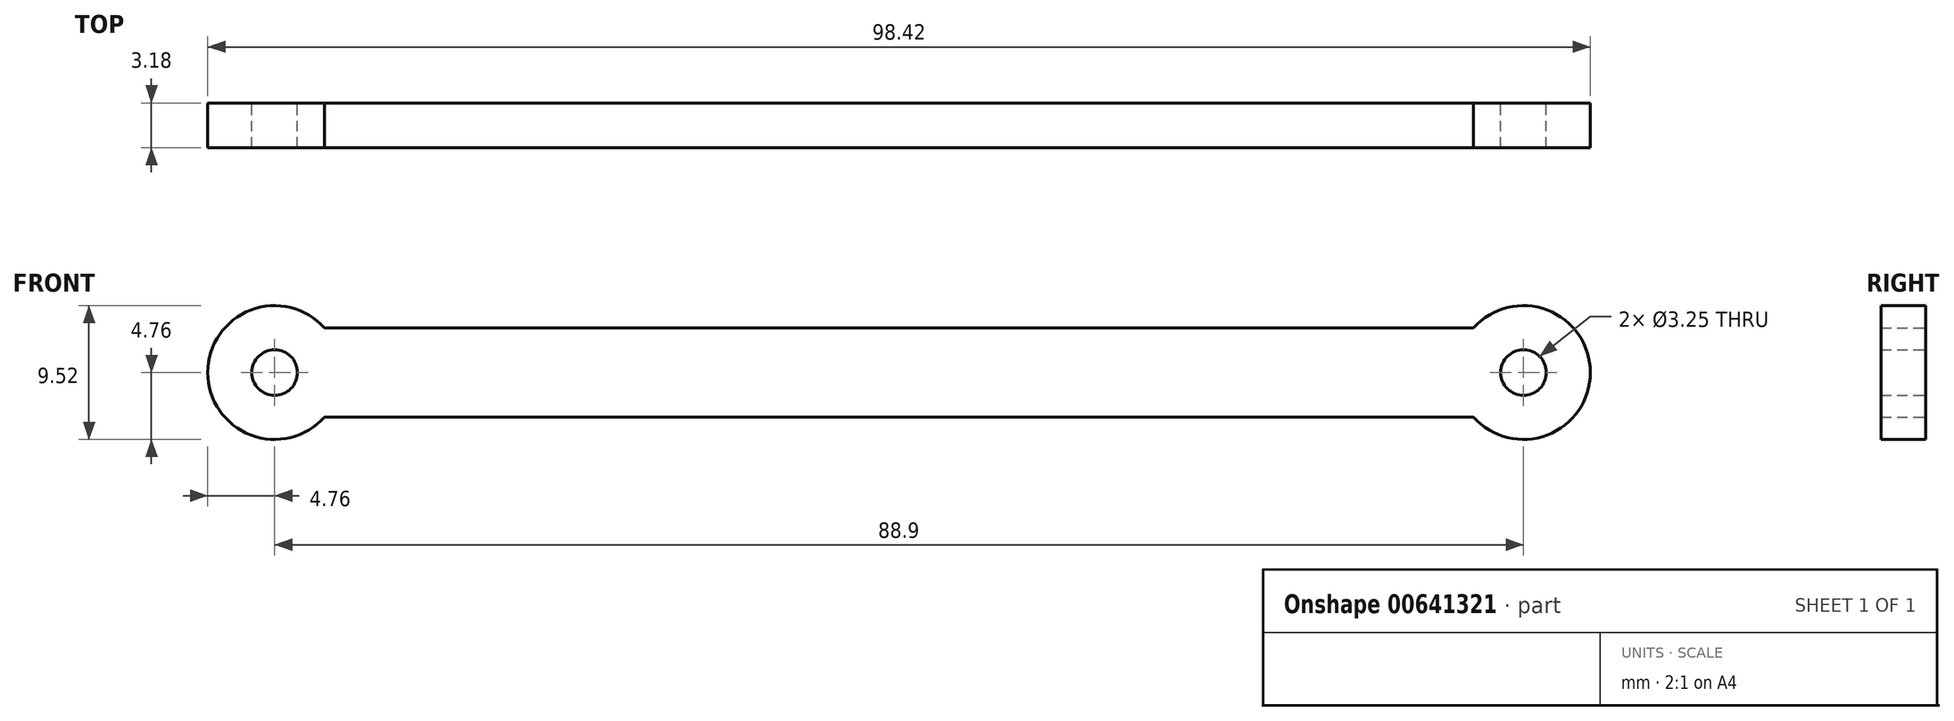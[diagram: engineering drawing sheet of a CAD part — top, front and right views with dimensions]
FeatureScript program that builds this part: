
annotation { "Feature Type Name" : "Feature", "Feature Type Description" : "" }
export const myFeature = defineFeature(function(context is Context, id is Id, definition is map)
    precondition{}
    {
        {
            var Q0;
            Q0=qCreatedBy(makeId("Front.planeOp"),FACE);
            var sketch = newSketch(context, id + "F0", { "sketchPlane" : qUnion([Q0])});
            skLineSegment(sketch, "E0", {"start": v(0, 0) * mm, "end": v(88.9, 0) * mm});
            skCircle(sketch, "E1", {"center": v(0, 0) * mm, "radius": 4.76 * mm});
            skCircle(sketch, "E2", {"center": v(88.9, 0) * mm, "radius": 4.76 * mm});
            skLineSegment(sketch, "E3.0", {"start": v(3.55, 3.18) * mm, "end": v(85.35, 3.18) * mm});
            skLineSegment(sketch, "E4.MirrorCS", {"start": v(3.55, -3.18) * mm, "end": v(85.35, -3.18) * mm});
            skPoint(sketch, "E5.orphan", {"position": v(88.9, -3.18) * mm});
            skPoint(sketch, "E6.orphan", {"position": v(88.9, 3.18) * mm});
            skPoint(sketch, "E7.orphan", {"position": v(0, 3.18) * mm});
            skPoint(sketch, "E8.orphan", {"position": v(0, -3.18) * mm});
            skCircle(sketch, "E9", {"center": v(0, 0) * mm, "radius": 1.63 * mm});
            skCircle(sketch, "E10", {"center": v(88.9, 0) * mm, "radius": 1.63 * mm});
            skSolve(sketch);
        }
        {
            var Q0;
            Q0 = qSketchRegion(id + "F0", true);
            extrude(context, id + "F1", {"entities" : qUnion([Q0]), "depth" : 3.17 * mm, "offsetDistance" : 25.4 * mm});
        }
    });
